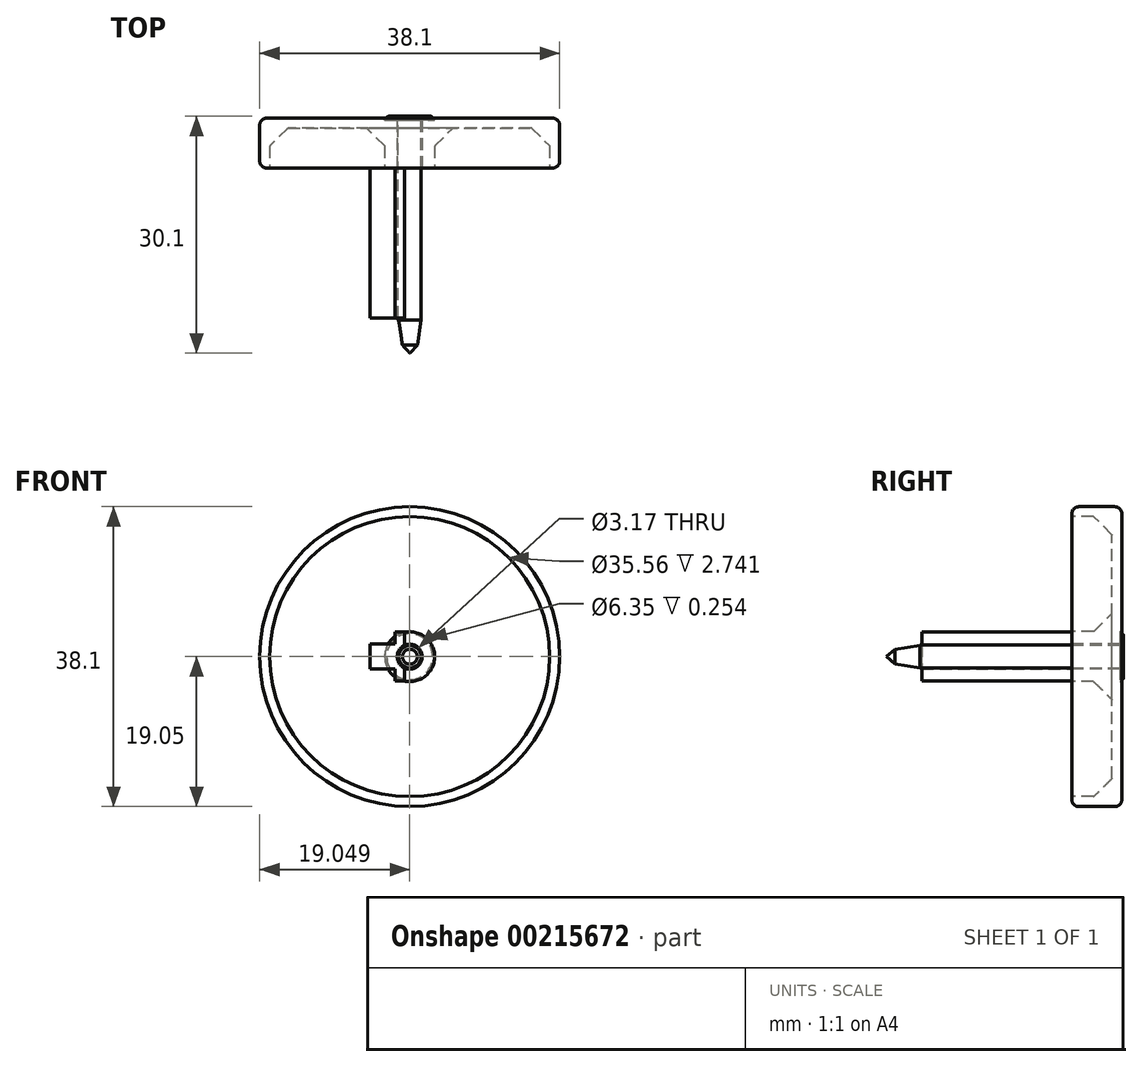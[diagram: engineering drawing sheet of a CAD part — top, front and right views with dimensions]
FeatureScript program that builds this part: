
annotation { "Feature Type Name" : "Feature", "Feature Type Description" : "" }
export const myFeature = defineFeature(function(context is Context, id is Id, definition is map)
    precondition{}
    {
        {
            var Q0;
            Q0=qCreatedBy(makeId("Front.planeOp"),FACE);
            var sketch = newSketch(context, id + "F0", { "sketchPlane" : qUnion([Q0])});
            skCircle(sketch, "E0", {"center": v(0.63, 0) * mm, "radius": 19.05 * mm});
            skSolve(sketch);
        }
        {
            var Q0;
            Q0=makeQuery(id+"F0.imprint","IMPRINT",FACE,{"disambiguationData":[TD([[makeQuery(id+"F0.imprint","IMPRINT",EDGE,{"derivedFrom":sQuery(id+"F0.wireOp",EDGE,"E0")}),1.0]])]});
            extrude(context, id + "F1", {"entities" : qUnion([Q0]), "depth" : 6.35 * mm});
        }
        {
            var Q0;
            Q0=makeQuery(id+"F1.opExtrude","CAP_FACE",FACE,{"disambiguationData":[OSD([sQuery(id+"F0.wireOp",EDGE,"E0")])],"isStart":false});
            var sketch = newSketch(context, id + "F2", { "sketchPlane" : qUnion([Q0])});
            skCircle(sketch, "E1", {"center": v(0.63, 0) * mm, "radius": 17.78 * mm});
            skCircle(sketch, "E2", {"center": v(0.63, 0) * mm, "radius": 3.18 * mm});
            skSolve(sketch);
        }
        {
            var Q0;
            Q0=makeQuery(id+"F2.imprint","IMPRINT",FACE,{"disambiguationData":[TD([[makeQuery(id+"F2.imprint","IMPRINT",EDGE,{"derivedFrom":sQuery(id+"F2.wireOp",EDGE,"E1")}),1.0]])]});
            extrude(context, id + "F3", {"entities" : qUnion([Q0]), "operationType" : NewBodyOperationType.REMOVE, "oppositeDirection" : true, "depth" : 5.08 * mm});
        }
        {
            var Q0;
            Q0=makeQuery(id+"F3.boolean.opBoolean","SPLIT",FACE,{"disambiguationData":[TD([makeQuery(id+"F3.opExtrude","SWEPT_FACE",FACE,{"disambiguationData":[OSD([sQuery(id+"F2.wireOp",EDGE,"E2")])]})])],"derivedFrom":makeQuery(id+"F1.opExtrude","CAP_FACE",FACE,{"disambiguationData":[OSD([sQuery(id+"F0.wireOp",EDGE,"E0")])],"isStart":false})});
            var sketch = newSketch(context, id + "F4", { "sketchPlane" : qUnion([Q0])});
            skCircle(sketch, "E3", {"center": v(0.63, 0) * mm, "radius": 1.59 * mm});
            skSolve(sketch);
        }
        {
            var Q0;
            Q0 = qSketchRegion(id + "F4", true);
            var Q1;
            Q1=makeQuery(id+"F1.opExtrude","CAP_FACE",FACE,{"disambiguationData":[OSD([sQuery(id+"F0.wireOp",EDGE,"E0")])],"isStart":true});
            extrude(context, id + "F5", {"entities" : qUnion([Q0]), "operationType" : NewBodyOperationType.REMOVE, "endBound" : BoundingType.UP_TO_SURFACE, "oppositeDirection" : true, "endBoundEntityFace" : qUnion([Q1]), "depth" : 25.4 * mm});
        }
        {
            var Q0;
            Q0=makeQuery(id+"F1.opExtrude","CAP_FACE",FACE,{"disambiguationData":[OSD([sQuery(id+"F0.wireOp",EDGE,"E0")])],"isStart":true});
            var sketch = newSketch(context, id + "F6", { "sketchPlane" : qUnion([Q0])});
            skCircle(sketch, "E4", {"center": v(-0.63, 0) * mm, "radius": 3.18 * mm});
            skSolve(sketch);
        }
        {
            var Q0;
            Q0 = qSketchRegion(id + "F6", true);
            extrude(context, id + "F7", {"entities" : qUnion([Q0]), "operationType" : NewBodyOperationType.REMOVE, "oppositeDirection" : true, "depth" : 0.25 * mm});
        }
        {
            var Q0;
            Q0=makeQuery(id+"F7.boolean.opBoolean","COPY",FACE,{"derivedFrom":makeQuery(id+"F7.opExtrude","CAP_FACE",FACE,{"disambiguationData":[OSD([sQuery(id+"F6.wireOp",EDGE,"E4")])],"isStart":false})});
            var sketch = newSketch(context, id + "F8", { "sketchPlane" : qUnion([Q0])});
            skCircle(sketch, "E5", {"center": v(-0.63, 0) * mm, "radius": 1.46 * mm});
            skSolve(sketch);
        }
        {
            var Q0;
            Q0 = qSketchRegion(id + "F8", true);
            extrude(context, id + "F9", {"entities" : qUnion([Q0]), "oppositeDirection" : true, "depth" : 25.4 * mm});
        }
        {
            var Q0;
            Q0=qCreatedBy(makeId("Top.planeOp"),FACE);
            var sketch = newSketch(context, id + "F10", { "sketchPlane" : qUnion([Q0])});
            skLineSegment(sketch, "E6", {"start": v(0.66, -25.65) * mm, "end": v(0.66, -29.87) * mm});
            skLineSegment(sketch, "E7", {"start": v(0.66, -29.87) * mm, "end": v(1.6, -28.83) * mm});
            skLineSegment(sketch, "E8", {"start": v(1.6, -28.83) * mm, "end": v(2.09, -25.65) * mm});
            skLineSegment(sketch, "E9", {"start": v(2.09, -25.65) * mm, "end": v(0.66, -25.65) * mm});
            skSolve(sketch);
        }
        {
            var Q0;
            Q0=makeQuery(id+"F10.imprint","IMPRINT",FACE,{"disambiguationData":[TD([[makeQuery(id+"F10.imprint","IMPRINT",EDGE,{"derivedFrom":sQuery(id+"F10.wireOp",EDGE,"E6")}),1.0]])]});
            var Q1;
            Q1=sQuery(id+"F10.wireOp",EDGE,"E6");
            revolve(context, id + "F11", {"operationType" : NewBodyOperationType.ADD, "entities" : qUnion([Q0]), "axis" : qUnion([Q1]), "revolveType" : RevolveType.FULL});
        }
        {
            var Q0;
            Q0=makeQuery(id+"F9.opExtrude","CAP_FACE",FACE,{"disambiguationData":[OSD([sQuery(id+"F8.wireOp",EDGE,"E5")])],"isStart":true});
            var sketch = newSketch(context, id + "F12", { "sketchPlane" : qUnion([Q0])});
            skCircle(sketch, "E10", {"center": v(-0.63, 0) * mm, "radius": 2.92 * mm});
            skSolve(sketch);
        }
        {
            var Q0;
            Q0 = qSketchRegion(id + "F12", true);
            extrude(context, id + "F13", {"entities" : qUnion([Q0]), "depth" : 0.48 * mm});
        }
        {
            var Q0;
            Q0=makeQuery(id+"F13.opExtrude","CAP_EDGE",EDGE,{"disambiguationData":[OSD([sQuery(id+"F12.wireOp",EDGE,"E10")])],"isStart":false});
            var Q1;
            Q1=makeQuery(id+"F7.boolean.opBoolean","COPY",EDGE,{"derivedFrom":makeQuery(id+"F7.opExtrude","CAP_EDGE",EDGE,{"disambiguationData":[OSD([sQuery(id+"F6.wireOp",EDGE,"E4")])],"isStart":true})});
            fillet(context, id + "F14", {"entities" : qUnion([Q0, Q1]), "radius" : 0.25 * mm, "tangentPropagation" : true, "allowEdgeOverflow" : false});
        }
        {
            var Q0;
            Q0=makeQuery(id+"F1.opExtrude","CAP_EDGE",EDGE,{"disambiguationData":[OSD([sQuery(id+"F0.wireOp",EDGE,"E0")])],"isStart":true});
            var Q1;
            Q1=makeQuery(id+"F1.opExtrude","CAP_EDGE",EDGE,{"disambiguationData":[OSD([sQuery(id+"F0.wireOp",EDGE,"E0")])],"isStart":false});
            fillet(context, id + "F15", {"entities" : qUnion([Q0, Q1]), "radius" : 0.89 * mm, "tangentPropagation" : true, "allowEdgeOverflow" : false});
        }
        {
            var Q0;
            Q0=makeQuery(id+"F3.boolean.opBoolean","COPY",FACE,{"derivedFrom":makeQuery(id+"F3.opExtrude","CAP_FACE",FACE,{"disambiguationData":[OSD([sQuery(id+"F2.wireOp",EDGE,"E1"),sQuery(id+"F2.wireOp",EDGE,"E2")])],"isStart":false})});
            chamfer(context, id + "F16", {"entities" : qUnion([Q0]), "width" : 2.3 * mm, "tangentPropagation" : true});
        }
        {
            var Q0;
            {var subQ0=sQuery(id+"F2.wireOp",EDGE,"E1");Q0=makeQuery(id+"F16.opChamfer","BLEND_EDGE",EDGE,{"blendedFrom":[makeQuery(id+"F3.boolean.opBoolean","COPY",EDGE,{"derivedFrom":makeQuery(id+"F3.opExtrude","CAP_EDGE",EDGE,{"disambiguationData":[OSD([subQ0])],"isStart":false})}),makeQuery(id+"F3.boolean.opBoolean","COPY",FACE,{"derivedFrom":makeQuery(id+"F3.opExtrude","CAP_FACE",FACE,{"disambiguationData":[OSD([subQ0,sQuery(id+"F2.wireOp",EDGE,"E2")])],"isStart":false})})],"blendedInto":[makeQuery(id+"F3.boolean.opBoolean","COPY",FACE,{"derivedFrom":makeQuery(id+"F3.opExtrude","CAP_FACE",FACE,{"disambiguationData":[OSD([subQ0,sQuery(id+"F2.wireOp",EDGE,"E2")])],"isStart":false})})]});}
            var Q1;
            {var subQ0=sQuery(id+"F2.wireOp",EDGE,"E2");Q1=makeQuery(id+"F16.opChamfer","BLEND_EDGE",EDGE,{"blendedFrom":[makeQuery(id+"F3.boolean.opBoolean","COPY",EDGE,{"derivedFrom":makeQuery(id+"F3.opExtrude","CAP_EDGE",EDGE,{"disambiguationData":[OSD([subQ0])],"isStart":false})}),makeQuery(id+"F3.boolean.opBoolean","COPY",FACE,{"derivedFrom":makeQuery(id+"F3.opExtrude","CAP_FACE",FACE,{"disambiguationData":[OSD([sQuery(id+"F2.wireOp",EDGE,"E1"),subQ0])],"isStart":false})})],"blendedInto":[makeQuery(id+"F3.boolean.opBoolean","COPY",FACE,{"derivedFrom":makeQuery(id+"F3.opExtrude","CAP_FACE",FACE,{"disambiguationData":[OSD([sQuery(id+"F2.wireOp",EDGE,"E1"),subQ0])],"isStart":false})})]});}
            var Q2;
            {var subQ0=sQuery(id+"F2.wireOp",EDGE,"E2");Q2=makeQuery(id+"F16.opChamfer","BLEND_EDGE",EDGE,{"blendedFrom":[makeQuery(id+"F3.boolean.opBoolean","COPY",EDGE,{"derivedFrom":makeQuery(id+"F3.opExtrude","CAP_EDGE",EDGE,{"disambiguationData":[OSD([subQ0])],"isStart":false})}),makeQuery(id+"F3.boolean.opBoolean","COPY",FACE,{"derivedFrom":makeQuery(id+"F3.opExtrude","SWEPT_FACE",FACE,{"disambiguationData":[OSD([subQ0])]})})],"blendedInto":[makeQuery(id+"F3.boolean.opBoolean","COPY",FACE,{"derivedFrom":makeQuery(id+"F3.opExtrude","SWEPT_FACE",FACE,{"disambiguationData":[OSD([subQ0])]})})]});}
            var Q3;
            {var subQ0=sQuery(id+"F2.wireOp",EDGE,"E1");Q3=makeQuery(id+"F16.opChamfer","BLEND_EDGE",EDGE,{"blendedFrom":[makeQuery(id+"F3.boolean.opBoolean","COPY",EDGE,{"derivedFrom":makeQuery(id+"F3.opExtrude","CAP_EDGE",EDGE,{"disambiguationData":[OSD([subQ0])],"isStart":false})}),makeQuery(id+"F3.boolean.opBoolean","COPY",FACE,{"derivedFrom":makeQuery(id+"F3.opExtrude","SWEPT_FACE",FACE,{"disambiguationData":[OSD([subQ0])]})})],"blendedInto":[makeQuery(id+"F3.boolean.opBoolean","COPY",FACE,{"derivedFrom":makeQuery(id+"F3.opExtrude","SWEPT_FACE",FACE,{"disambiguationData":[OSD([subQ0])]})})]});}
            fillet(context, id + "F17", {"entities" : qUnion([Q0, Q1, Q2, Q3]), "radius" : 0.13 * mm, "tangentPropagation" : true, "allowEdgeOverflow" : false});
        }
        {
            var Q0;
            Q0=makeQuery(id+"F3.boolean.opBoolean","SPLIT",FACE,{"disambiguationData":[TD([makeQuery(id+"F3.opExtrude","SWEPT_FACE",FACE,{"disambiguationData":[OSD([sQuery(id+"F2.wireOp",EDGE,"E2")])]})])],"derivedFrom":makeQuery(id+"F1.opExtrude","CAP_FACE",FACE,{"disambiguationData":[OSD([sQuery(id+"F0.wireOp",EDGE,"E0")])],"isStart":false})});
            var sketch = newSketch(context, id + "F18", { "sketchPlane" : qUnion([Q0])});
            skLineSegment(sketch, "E11.bottom", {"start": v(0, 3.11) * mm, "end": v(-1.22, 3.11) * mm});
            skLineSegment(sketch, "E11.top", {"start": v(0, -3.11) * mm, "end": v(-1.22, -3.11) * mm});
            skLineSegment(sketch, "E11.left", {"start": v(0, 3.11) * mm, "end": v(0, 1.46) * mm});
            skArc(sketch, "E12.0", {"start": v(0, 1.46) * mm, "mid": v(-0.96, 0) * mm, "end": v(0, -1.46) * mm});
            skLineSegment(sketch, "E13.trimOffspring", {"start": v(0, -1.46) * mm, "end": v(0, -3.11) * mm});
            skLineSegment(sketch, "E14", {"start": v(-1.22, -3.11) * mm, "end": v(-1.22, -1.59) * mm});
            skLineSegment(sketch, "E15", {"start": v(-1.22, -1.59) * mm, "end": v(-4.4, -1.59) * mm});
            skLineSegment(sketch, "E16", {"start": v(-4.4, -1.59) * mm, "end": v(-4.4, 1.59) * mm});
            skLineSegment(sketch, "E17", {"start": v(-4.4, 1.59) * mm, "end": v(-1.22, 1.59) * mm});
            skLineSegment(sketch, "E18", {"start": v(-1.22, 1.59) * mm, "end": v(-1.22, 3.11) * mm});
            skSolve(sketch);
        }
        {
            var Q0;
            Q0 = qSketchRegion(id + "F18", true);
            extrude(context, id + "F19", {"entities" : qUnion([Q0]), "depth" : 19.05 * mm});
        }
    });
